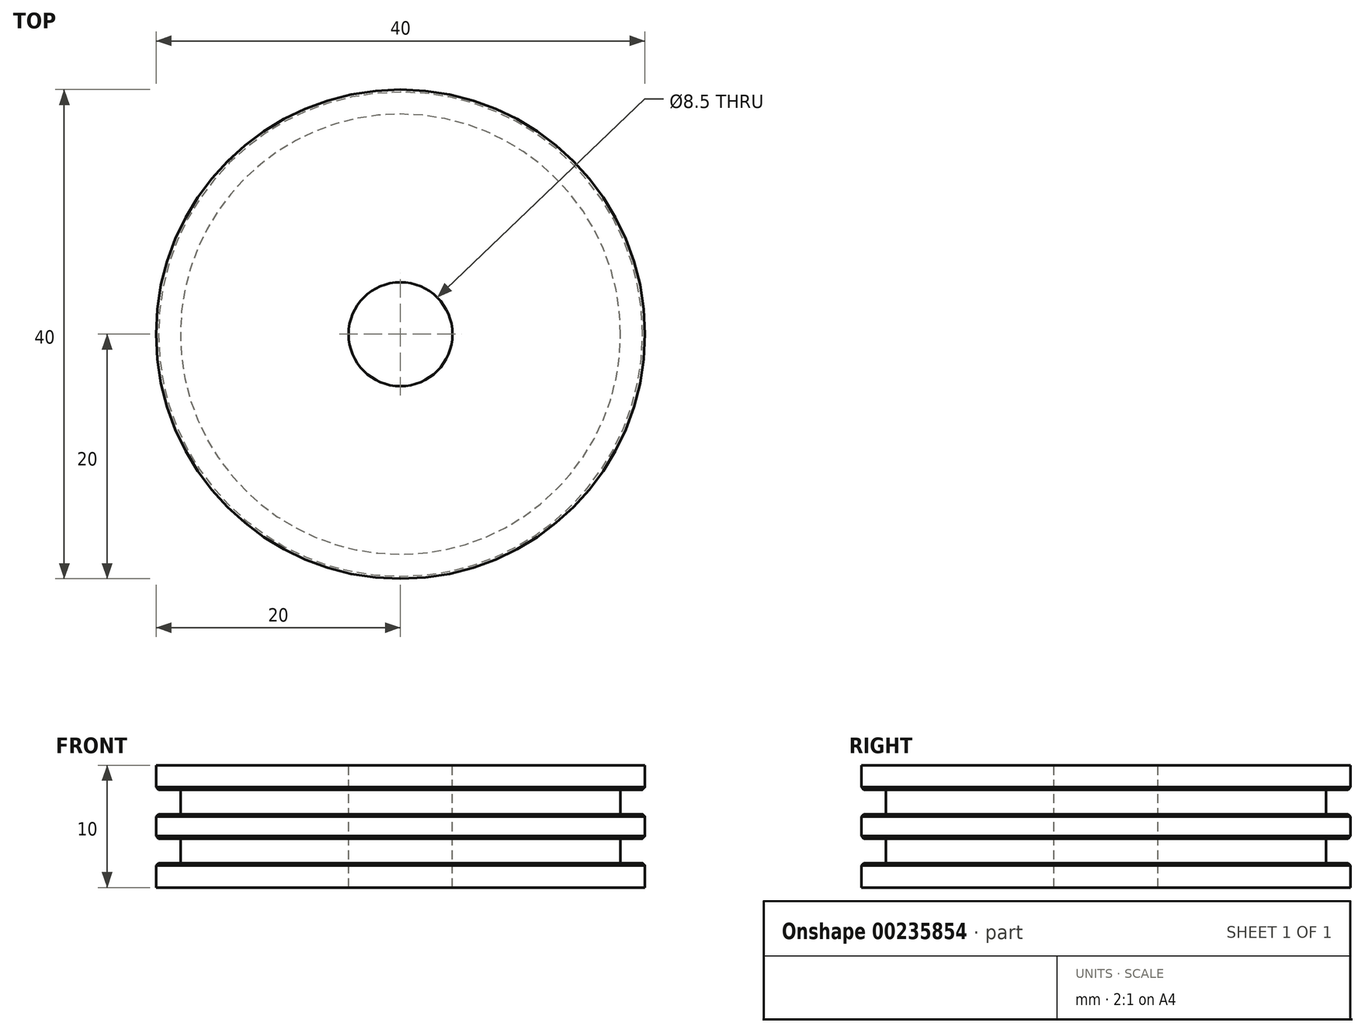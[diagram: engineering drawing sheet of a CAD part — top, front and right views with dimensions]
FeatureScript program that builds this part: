
annotation { "Feature Type Name" : "Feature", "Feature Type Description" : "" }
export const myFeature = defineFeature(function(context is Context, id is Id, definition is map)
    precondition{}
    {
        {
            var Q0;
            Q0=qCreatedBy(makeId("Front.planeOp"),FACE);
            var sketch = newSketch(context, id + "F0", { "sketchPlane" : qUnion([Q0])});
            skLineSegment(sketch, "E0", {"start": v(0, 0) * mm, "end": v(0, -10) * mm, "construction": true});
            skLineSegment(sketch, "E1.0", {"start": v(20, 0) * mm, "end": v(20, -2) * mm});
            skLineSegment(sketch, "E2.0", {"start": v(18, -2) * mm, "end": v(18, -4) * mm});
            skLineSegment(sketch, "E3", {"start": v(4.25, -10) * mm, "end": v(20, -10) * mm});
            skLineSegment(sketch, "E4.0", {"start": v(18, -8) * mm, "end": v(20, -8) * mm});
            skLineSegment(sketch, "E5.0", {"start": v(18, -6) * mm, "end": v(20, -6) * mm});
            skLineSegment(sketch, "E6.0", {"start": v(18, -4) * mm, "end": v(20, -4) * mm});
            skLineSegment(sketch, "E7.0", {"start": v(18, -2) * mm, "end": v(20, -2) * mm});
            skLineSegment(sketch, "E8.0", {"start": v(4.25, 0) * mm, "end": v(20, 0) * mm});
            skLineSegment(sketch, "E9.trimOffspring", {"start": v(20, -4) * mm, "end": v(20, -6) * mm});
            skLineSegment(sketch, "E10.trimOffspring", {"start": v(20, -8) * mm, "end": v(20, -10) * mm});
            skLineSegment(sketch, "E11.trimOffspring", {"start": v(18, -6) * mm, "end": v(18, -8) * mm});
            skLineSegment(sketch, "E12.0", {"start": v(4.25, 0) * mm, "end": v(4.25, -10) * mm});
            skSolve(sketch);
        }
        {
            var Q0;
            Q0=makeQuery(id+"F0.imprint","IMPRINT",FACE,{"disambiguationData":[TD([[makeQuery(id+"F0.imprint","IMPRINT",EDGE,{"derivedFrom":sQuery(id+"F0.wireOp",EDGE,"E1.0")}),-1.0]])]});
            var Q1;
            Q1=sQuery(id+"F0.wireOp",EDGE,"E0");
            revolve(context, id + "F1", {"entities" : qUnion([Q0]), "axis" : qUnion([Q1]), "revolveType" : RevolveType.FULL});
        }
        {
            var Q0;
            Q0=makeQuery(id+"F1.opRevolve","SWEPT_EDGE",EDGE,{"disambiguationData":[OSD([sQuery(id+"F0.wireOp",EDGE,"E1.0"),sQuery(id+"F0.wireOp",EDGE,"E7.0")])]});
            var Q1;
            Q1=makeQuery(id+"F1.opRevolve","SWEPT_EDGE",EDGE,{"disambiguationData":[OSD([sQuery(id+"F0.wireOp",EDGE,"E6.0"),sQuery(id+"F0.wireOp",EDGE,"E9.trimOffspring")])]});
            var Q2;
            Q2=makeQuery(id+"F1.opRevolve","SWEPT_EDGE",EDGE,{"disambiguationData":[OSD([sQuery(id+"F0.wireOp",EDGE,"E4.0"),sQuery(id+"F0.wireOp",EDGE,"E10.trimOffspring")])]});
            var Q3;
            Q3=makeQuery(id+"F1.opRevolve","SWEPT_EDGE",EDGE,{"disambiguationData":[OSD([sQuery(id+"F0.wireOp",EDGE,"E5.0"),sQuery(id+"F0.wireOp",EDGE,"E9.trimOffspring")])]});
            chamfer(context, id + "F2", {"entities" : qUnion([Q0, Q1, Q2, Q3]), "chamferType" : ChamferType.OFFSET_ANGLE, "width" : .2 * mm, "oppositeDirection" : false, "angle" : 45 * degree, "tangentPropagation" : true});
        }
    });
